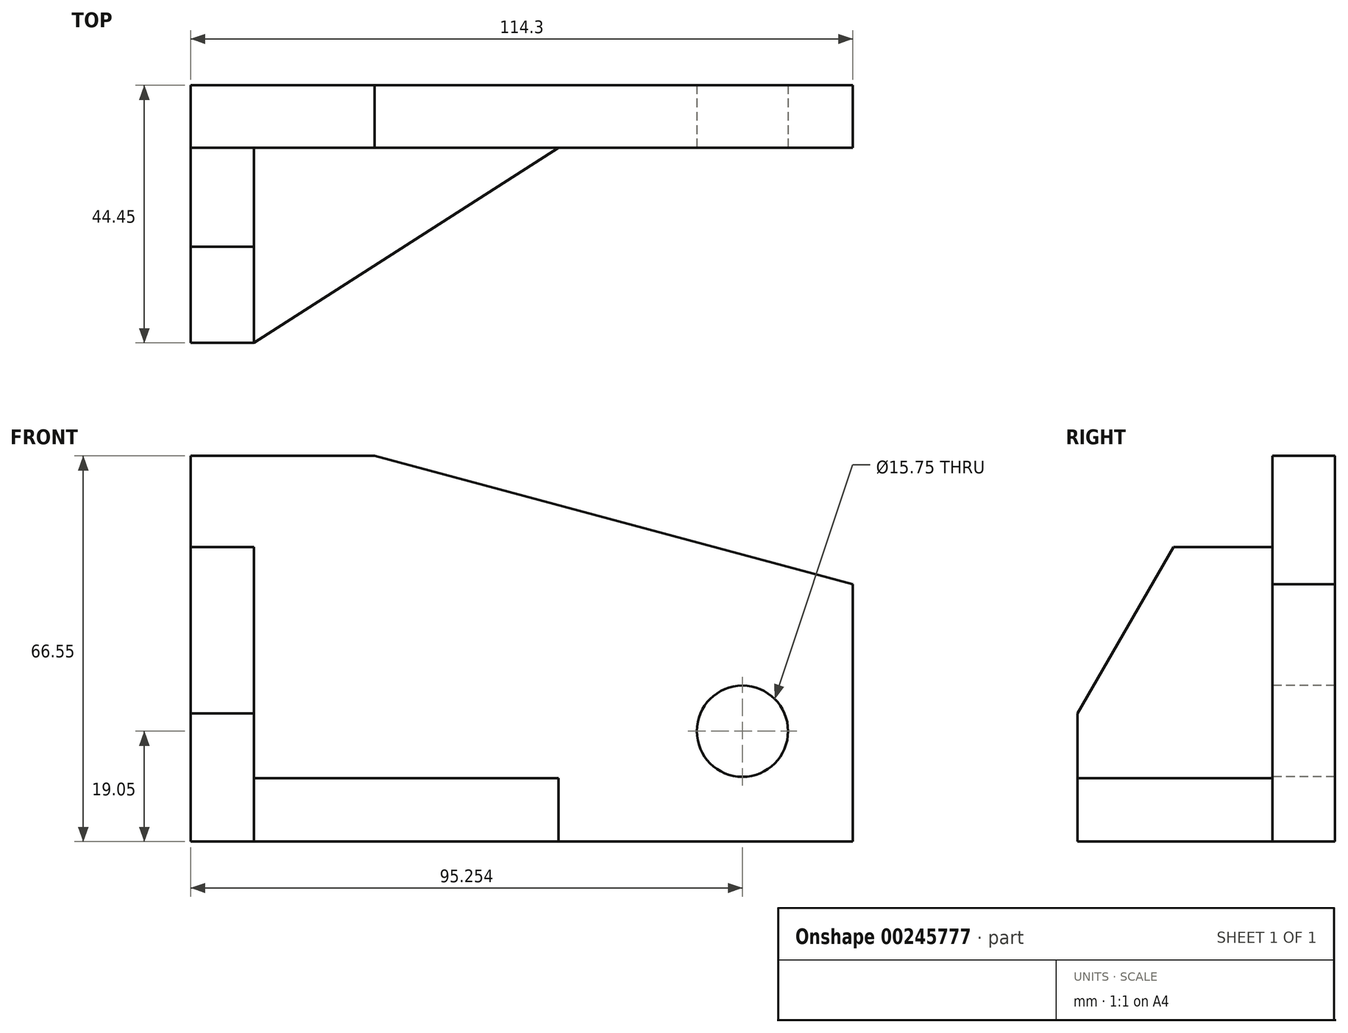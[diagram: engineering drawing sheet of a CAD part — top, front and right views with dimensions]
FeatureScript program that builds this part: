
annotation { "Feature Type Name" : "Feature", "Feature Type Description" : "" }
export const myFeature = defineFeature(function(context is Context, id is Id, definition is map)
    precondition{}
    {
        {
            var Q0;
            Q0=qCreatedBy(makeId("Top.planeOp"),FACE);
            var sketch = newSketch(context, id + "F0", { "sketchPlane" : qUnion([Q0])});
            skLineSegment(sketch, "E0", {"start": v(-76.5, 44.45) * mm, "end": v(37.8, 44.45) * mm});
            skLineSegment(sketch, "E1", {"start": v(-76.5, 44.45) * mm, "end": v(-76.5, 0) * mm});
            skLineSegment(sketch, "E2", {"start": v(37.8, 44.45) * mm, "end": v(37.8, 33.7) * mm});
            skLineSegment(sketch, "E3", {"start": v(-76.5, 33.7) * mm, "end": v(37.8, 33.7) * mm});
            skLineSegment(sketch, "E4", {"start": v(-65.57, 33.7) * mm, "end": v(-65.57, 0) * mm});
            skLineSegment(sketch, "E5", {"start": v(-65.57, 0) * mm, "end": v(-76.5, 0) * mm});
            skLineSegment(sketch, "E6", {"start": v(-65.57, 0) * mm, "end": v(-13, 33.7) * mm});
            skSolve(sketch);
        }
        {
            var Q0;
            Q0=makeQuery(id+"F0.imprint","IMPRINT",FACE,{"disambiguationData":[TD([[makeQuery(id+"F0.imprint","IMPRINT",EDGE,{"derivedFrom":sQuery(id+"F0.wireOp",EDGE,"E0")}),-1.0]])]});
            extrude(context, id + "F1", {"entities" : qUnion([Q0]), "depth" : 66.55 * mm});
        }
        {
            var Q0;
            {var subQ0=sQuery(id+"F0.wireOp",EDGE,"E3");Q0=makeQuery(id+"F0.imprint","IMPRINT",FACE,{"disambiguationData":[TD([[makeQuery(id+"F0.imprint","IMPRINT",EDGE,{"derivedFrom":subQ0}),-1.0]])]});}
            extrude(context, id + "F2", {"entities" : qUnion([Q0]), "operationType" : NewBodyOperationType.ADD, "depth" : 10.92 * mm});
        }
        {
            var Q0;
            Q0=makeQuery(id+"F1.opExtrude","SWEPT_FACE",FACE,{"disambiguationData":[OSD([sQuery(id+"F0.wireOp",EDGE,"1Icrnbh3-ILkV-PCb3-Ztrl-EcbT0tqGkJC8"),sQuery(id+"F0.wireOp",EDGE,"EJdwOO8Y-dzCA-DjsJ-QD7H-jWzyDIeuyTYc"),sQuery(id+"F0.wireOp",EDGE,"E3")])]});
            var sketch = newSketch(context, id + "F3", { "sketchPlane" : qUnion([Q0])});
            skLineSegment(sketch, "E7", {"start": v(37.8, 0) * mm, "end": v(18.75, 0) * mm});
            skLineSegment(sketch, "E8", {"start": v(18.75, 0) * mm, "end": v(18.75, 19.05) * mm});
            skCircle(sketch, "E9", {"center": v(18.75, 19.05) * mm, "radius": 7.87 * mm});
            skLineSegment(sketch, "E10", {"start": v(-44.75, 66.55) * mm, "end": v(37.8, 44.43) * mm});
            skSolve(sketch);
        }
        {
            var Q0;
            Q0=makeQuery(id+"F3.imprint","IMPRINT",FACE,{"disambiguationData":[TD([[makeQuery(id+"F3.imprint","IMPRINT",EDGE,{"derivedFrom":sQuery(id+"F3.wireOp",EDGE,"E9")}),1.0]])]});
            extrude(context, id + "F4", {"entities" : qUnion([Q0]), "operationType" : NewBodyOperationType.REMOVE, "endBound" : BoundingType.THROUGH_ALL, "oppositeDirection" : true, "depth" : 127 * mm});
        }
        {
            var Q0;
            {var subQ4=sQuery(id+"F0.wireOp",EDGE,"E4");Q0=makeQuery(id+"F0.imprint","IMPRINT",FACE,{"disambiguationData":[TD([[makeQuery(id+"F0.imprint","IMPRINT",EDGE,{"derivedFrom":subQ4}),-1.0]])]});}
            extrude(context, id + "F5", {"entities" : qUnion([Q0]), "operationType" : NewBodyOperationType.ADD, "depth" : 50.8 * mm});
        }
        {
            var Q0;
            Q0=makeQuery(id+"F5.opExtrude","SWEPT_FACE",FACE,{"disambiguationData":[OSD([sQuery(id+"F0.wireOp",EDGE,"E4")])]});
            var sketch = newSketch(context, id + "F6", { "sketchPlane" : qUnion([Q0])});
            skLineSegment(sketch, "E11", {"start": v(0, 0) * mm, "end": v(0, 22.1) * mm});
            skLineSegment(sketch, "E12", {"start": v(0, 22.1) * mm, "end": v(0, 50.8) * mm});
            skLineSegment(sketch, "E13", {"start": v(0, 22.1) * mm, "end": v(16.57, 50.8) * mm});
            skSolve(sketch);
        }
        {
            var Q0;
            {var subQ0=sQuery(id+"F6.wireOp",EDGE,"E12");Q0=makeQuery(id+"F6.imprint","IMPRINT",FACE,{"disambiguationData":[TD([[makeQuery(id+"F6.imprint","IMPRINT",EDGE,{"derivedFrom":subQ0}),1.0]])]});}
            extrude(context, id + "F7", {"entities" : qUnion([Q0]), "operationType" : NewBodyOperationType.REMOVE, "oppositeDirection" : true, "depth" : 127 * mm});
        }
        {
            var Q0;
            {var subQ0=sQuery(id+"F3.wireOp",EDGE,"E10");Q0=makeQuery(id+"F3.imprint","IMPRINT",FACE,{"disambiguationData":[TD([[makeQuery(id+"F3.imprint","IMPRINT",EDGE,{"derivedFrom":subQ0}),1.0]])]});}
            extrude(context, id + "F8", {"entities" : qUnion([Q0]), "operationType" : NewBodyOperationType.REMOVE, "oppositeDirection" : true, "depth" : 127 * mm});
        }
    });
